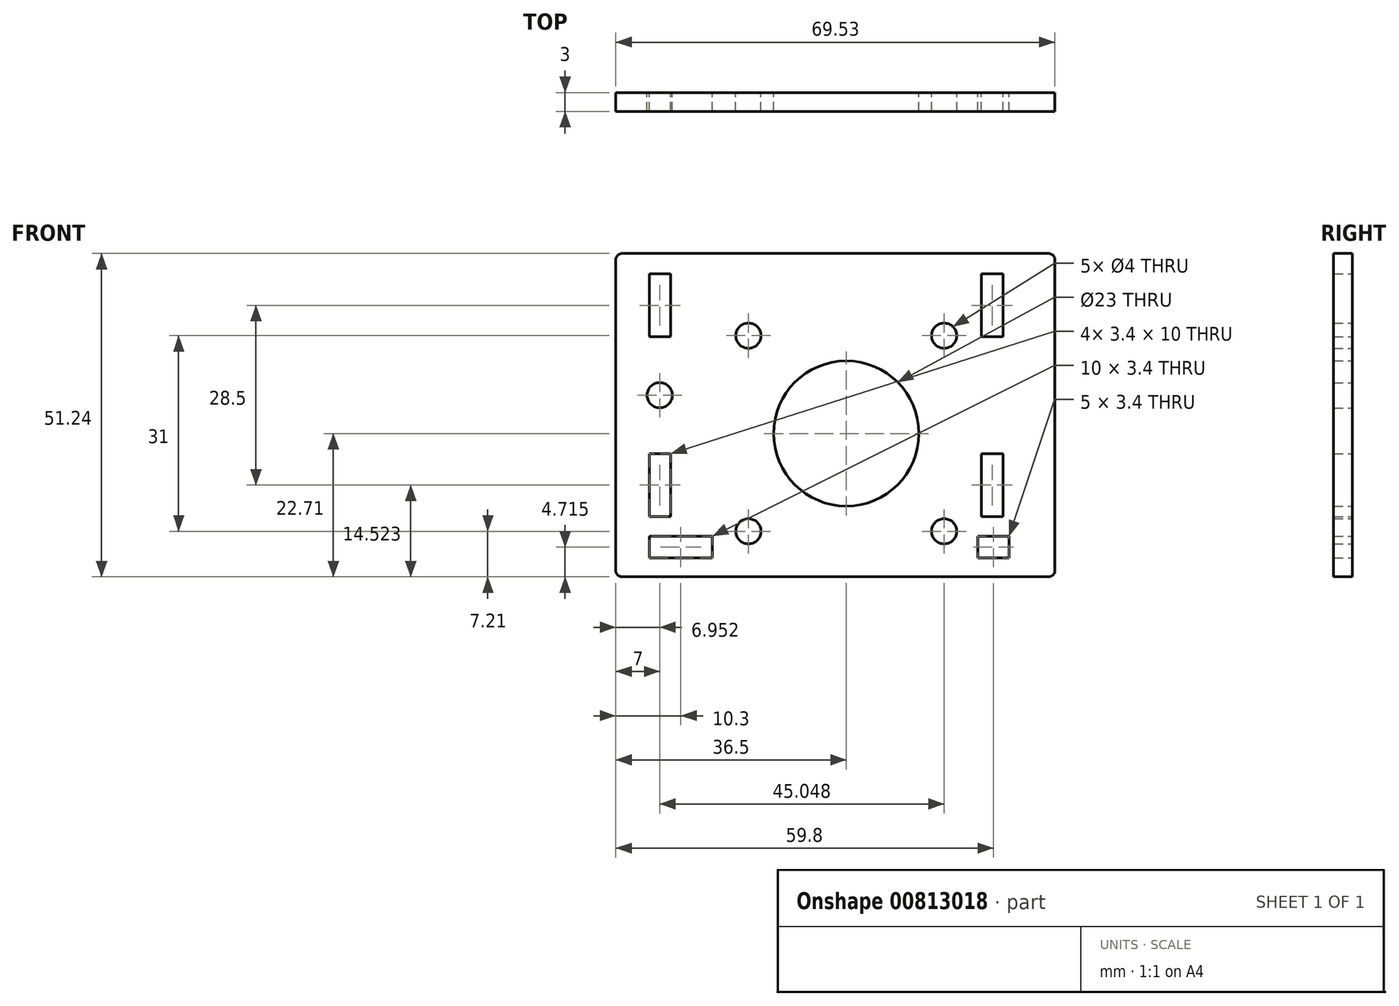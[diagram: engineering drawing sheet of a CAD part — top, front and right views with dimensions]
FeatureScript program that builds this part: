
annotation { "Feature Type Name" : "Feature", "Feature Type Description" : "" }
export const myFeature = defineFeature(function(context is Context, id is Id, definition is map)
    precondition{}
    {
        {
            var Q0;
            Q0=qCreatedBy(makeId("Front.planeOp"),FACE);
            var sketch = newSketch(context, id + "F0", { "sketchPlane" : qUnion([Q0])});
            skLineSegment(sketch, "E0.bottom", {"start": v(-14.3, 28.53) * mm, "end": v(53.23, 28.53) * mm});
            skLineSegment(sketch, "E0.top", {"start": v(-14.3, -22.71) * mm, "end": v(53.23, -22.71) * mm});
            skLineSegment(sketch, "E0.left", {"start": v(-15.3, 27.53) * mm, "end": v(-15.3, -21.71) * mm});
            skLineSegment(sketch, "E0.right", {"start": v(54.23, 27.53) * mm, "end": v(54.23, -21.71) * mm});
            skLineSegment(sketch, "E1.bottom", {"start": v(-10, -16.3) * mm, "end": v(0, -16.3) * mm});
            skLineSegment(sketch, "E1.top", {"start": v(-10, -19.7) * mm, "end": v(0, -19.7) * mm});
            skLineSegment(sketch, "E1.left", {"start": v(-10, -16.3) * mm, "end": v(-10, -19.7) * mm});
            skLineSegment(sketch, "E1.right", {"start": v(0, -16.3) * mm, "end": v(0, -19.7) * mm});
            skLineSegment(sketch, "E2.bottom", {"start": v(-10, 25.31) * mm, "end": v(-6.6, 25.31) * mm});
            skLineSegment(sketch, "E2.top", {"start": v(-10, 15.31) * mm, "end": v(-6.6, 15.31) * mm});
            skLineSegment(sketch, "E2.left", {"start": v(-10, 25.31) * mm, "end": v(-10, 15.31) * mm});
            skLineSegment(sketch, "E2.right", {"start": v(-6.6, 25.31) * mm, "end": v(-6.6, 15.31) * mm});
            skLineSegment(sketch, "E3.bottom", {"start": v(-10, -3.19) * mm, "end": v(-6.6, -3.19) * mm});
            skLineSegment(sketch, "E3.top", {"start": v(-10, -13.19) * mm, "end": v(-6.6, -13.19) * mm});
            skLineSegment(sketch, "E3.left", {"start": v(-10, -3.19) * mm, "end": v(-10, -13.19) * mm});
            skLineSegment(sketch, "E3.right", {"start": v(-6.6, -3.19) * mm, "end": v(-6.6, -13.19) * mm});
            skLineSegment(sketch, "E4.bottom", {"start": v(42.6, 25.31) * mm, "end": v(46, 25.31) * mm});
            skLineSegment(sketch, "E4.top", {"start": v(42.6, 15.31) * mm, "end": v(46, 15.31) * mm});
            skLineSegment(sketch, "E4.left", {"start": v(42.6, 25.31) * mm, "end": v(42.6, 15.31) * mm});
            skLineSegment(sketch, "E4.right", {"start": v(46, 25.31) * mm, "end": v(46, 15.31) * mm});
            skLineSegment(sketch, "E5.bottom", {"start": v(42.6, -3.19) * mm, "end": v(46, -3.19) * mm});
            skLineSegment(sketch, "E5.top", {"start": v(42.6, -13.19) * mm, "end": v(46, -13.19) * mm});
            skLineSegment(sketch, "E5.left", {"start": v(42.6, -3.19) * mm, "end": v(42.6, -13.19) * mm});
            skLineSegment(sketch, "E5.right", {"start": v(46, -3.19) * mm, "end": v(46, -13.19) * mm});
            skLineSegment(sketch, "E6.bottom", {"start": v(42, -16.3) * mm, "end": v(47, -16.3) * mm});
            skLineSegment(sketch, "E6.top", {"start": v(42, -19.7) * mm, "end": v(47, -19.7) * mm});
            skLineSegment(sketch, "E6.left", {"start": v(42, -16.3) * mm, "end": v(42, -19.7) * mm});
            skLineSegment(sketch, "E6.right", {"start": v(47, -16.3) * mm, "end": v(47, -19.7) * mm});
            skCircle(sketch, "E7", {"center": v(21.2, 0) * mm, "radius": 11.5 * mm});
            skCircle(sketch, "E8", {"center": v(36.7, 15.5) * mm, "radius": 2 * mm});
            skCircle(sketch, "E9", {"center": v(36.7, -15.5) * mm, "radius": 2 * mm});
            skCircle(sketch, "E10", {"center": v(5.7, -15.5) * mm, "radius": 2 * mm});
            skCircle(sketch, "E11", {"center": v(5.7, 15.5) * mm, "radius": 2 * mm});
            skPoint(sketch, "E12.visualSharp", {"position": v(-15.3, 28.53) * mm});
            skArc(sketch, "E12.filletArc", {"start": v(-14.3, 28.53) * mm, "mid": v(-15, 28.23) * mm, "end": v(-15.3, 27.53) * mm});
            skPoint(sketch, "E13.visualSharp", {"position": v(-15.3, -22.71) * mm});
            skArc(sketch, "E13.filletArc", {"start": v(-15.3, -21.71) * mm, "mid": v(-15, -22.42) * mm, "end": v(-14.3, -22.71) * mm});
            skPoint(sketch, "E14.visualSharp", {"position": v(54.23, -22.71) * mm});
            skArc(sketch, "E14.filletArc", {"start": v(53.23, -22.71) * mm, "mid": v(53.94, -22.42) * mm, "end": v(54.23, -21.71) * mm});
            skPoint(sketch, "E15.visualSharp", {"position": v(54.23, 28.53) * mm});
            skArc(sketch, "E15.filletArc", {"start": v(54.23, 27.53) * mm, "mid": v(53.94, 28.23) * mm, "end": v(53.23, 28.53) * mm});
            skCircle(sketch, "E16", {"center": v(-8.35, 6.06) * mm, "radius": 2 * mm});
            skSolve(sketch);
        }
        {
            var Q0;
            Q0 = qSketchRegion(id + "F0", true);
            extrude(context, id + "F1", {"entities" : qUnion([Q0]), "depth" : 3 * mm, "offsetDistance" : 25 * mm});
        }
    });
